# Revit family: xWELED_Ceiling Hosted_R16_V1.0
name_source: partatom
category: Lighting Fixtures
revit_build: Autodesk Revit 2016 (Build: 20150220_1215(x64)
units: mm (PartAtom-declared; Revit-internal decimal feet)

## family parameters
Always vertical = Yes
Cut with Voids When Loaded = No
Host = Ceiling
Light Source = Yes
OmniClass Number = 23.80.70.11
OmniClass Title = Luminaries for Internal Lighting
Part Type = Normal
Room Calculation Point = No
Round Connector Dimension = Use Diameter
Shared = No
Work Plane-Based = No

## types (11) — shared parameters
Charging Method = Intelligent current limited constant voltage charger
Color Filter = 16777215
Diffuser = (All directional inserts included in the box)
Dimensions L x W x H = 410mm x 100mm x 272mm
Dimming Lamp Color Temperature Shift = <None>
Operating Mode = Maintained
Operating Temperature = 1˚C to 40˚C
Tilt Angle = 90.00°

## per-type parameters (varying)
| type | AS/NZ2293 Classification | Battery | Catalogue Number | Construction | Description | IP Rating | Impact Rating | Lamp | Mounting | Operating Voltage | Photometric Web File | Power Consumption | Testing System | Viewing Distance |
| CWELED-ZW | C0=E2 C90=E2 |  | LWELED-ZW | Base Material: GRP
Diffuser Cover Material: Polycarbonate | LED L10 OPTIMUM Ceiling Mount IP65 Weatherproof Exit, 24 metre viewing Distance | IP65 | IK08 | 6 x high intensity, low energy LED, surface mounted onto a replaceable lamp bar - 100,000hour | Ceiling Mount, Single & Double Sided | 240V | ll19244-r01 - CWELED-ZW.IES | 2.7W (standby) 4.7W (max during 16 hour charge) | Zoneworks Computerised Testing |  |
| CWELED | C0=E2 C90=E2 | Lithium Iron Phosphate, 3.2V 1500mAh | CWELED | Polycarbonate Clear Cover, Glass Reinforced Nylon PA66 Base | LP Premium Weatherproof Emergency Exit, Enabled with Clevertest Plus | IP66/IP67 | IK10 | 6 x lLED lamp bar - 100,000 hours | Wall, Ceiling Mount, Single & Double Sided | 240V AC; 50Hz | ll19244-r01 - CWELED-ZW.IES | 2.6W (standby) 5.1W (max) | Clevertest Plus Enabled (not activated by default) | 24m |
| CWELED-A | C0=E2 C90=E2 | Lithium Iron Phosphate, 3.2V 1500mAh | CWELED-A | Acrylic Clear Cover, Glass Reinforced Nylon PA66 Base | LP Premium Weatherproof Emergency Exit with Acrylic Cover, Enabled with Clevertest Plus | IP66/IP67 | IK10 | 6 x lLED lamp bar - 100,000 hours | Wall, Ceiling Mount, Single & Double Sided | 240V AC; 50Hz | ll19244-r01 - CWELED-ZW.IES | 2.6W (standby) 5.1W (max) | Clevertest Plus Enabled (not activated by default) | 24m |
| CWELED-TP | C0=E2 C90=E2 | Lithium Iron Phosphate, 3.2V 1500mAh | CWELED-TP | Polycarbonate Cover, Glass Reinforced Nylon PA66 Base | LP Premium Weatherproof Emergency Exit and tamperproof screws, Enabled with Clevertest Plus | IP66/IP67 | IK10 | 6 x lLED lamp bar - 100,000 hours | Wall, Ceiling Mount, Single & Double Sided | 240V AC; 50Hz | ll19244-r01 - CWELED-ZW.IES | 2.6W (standby) 5.1W (max) | Clevertest Plus Enabled (not activated by default) | 24m |
| CWELED-DALI | C0=E2 C90=E2 | Lithium Iron Phosphate, 3.2V 1500mAh | CWELED-DALI | Polycarbonate Clear Cover, Glass Reinforced Nylon PA66 Base | LP Premium Weatherproof Emergency Exit | IP66/IP67 | IK10 | 6 x lLED lamp bar - 100,000 hours | Wall, Ceiling Mount, Single & Double Sided | 240V AC; 50Hz | ll19244-r01 - CWELED-ZW.IES | 2.6W (standby) 5.1W (max) | DALI Compatible | 24m |
| CWELED-DATA | C0=E2 C90=E2 | Lithium Iron Phosphate, 3.2V 1500mAh | CWELED-DATA | Polycarbonate Clear Cover, Glass Reinforced Nylon PA66 Base | LP Premium Weatherproof Emergency Exit | IP66/IP67 | IK10 | 6 x lLED lamp bar - 100,000 hours | Wall, Ceiling Mount, Single & Double Sided | 240V AC; 50Hz | ll19244-r01 - CWELED-ZW.IES | 2.6W (standby) 5.1W (max) | Zoneworks DATA | 24m |
| LWELED | C0=E2 C90=E2 | Lithium Nonophosphate, 3.3V 2500mAh | LWELED | Polycarbonate Clear Cover, Glass Reinforced Nylon PA66 Base | L10 Lithium Nanophosphate Weatherproof Emergency Exit, Enabled with Clevertest Plus | IP66/IP67 | IK10 | 6 x LED lamp bar - 100,000 hours | Wall, Ceiling Mount, Single & Double Sided | 240V AC; 50Hz | ll19243 - LWELED-ZW.IES | 2.7W (standby) 4.5W (max) | Clevertest Plus Enabled (not activated by default) | 24m |
| LWELED-ZW | C0=E2 C90=E2 | Lithium Nanophosphate, 3.3V 2500mAh | LWELED-ZW | Polycarbonate Clear Cover, Glass Reinforced Nylon PA66 Base | L10 Optimum Weatherproof Emergency Exit | IP66/IP67 | IK10 | 6 x LED lamp bar - 100,000 hours | Wall, Ceiling Mount, Single & Double Sided | 240V AC; 50Hz | ll19243 - LWELED-ZW.IES | 2.7W (standby) 4.5W (max) | Zoneworks Computer Testing | 24m |
| LWELED-DALI | C0=E2 C90=E2 | Lithium Nanophosphate, 3.3V 2500mAh | LWELED-DALI | Polycarbonate Clear Cover, Glass Reinforced Nylon PA66 Base | L10 Optimum Weatherproof Emergency Exit | IP66/IP67 | IK10 | 6 x LED lamp bar - 100,000 hours | Wall, Ceiling Mount, Single & Double Sided | 240V AC; 50Hz | ll19243 - LWELED-ZW.IES | 2.7W (standby) 4.5W (max) | DALI Compatible | 24m |
| LWELED-DATA | C0=E2 C90=E2 | Lithium Nanophosphate, 3.3V 2500mAh | LWELED-DATA | Polycarbonate Clear Cover, Glass Reinforced Nylon PA66 Base | L10 Optimum Weatherproof Emergency Exit | IP66/IP67 | IK10 | 6 x LED lamp bar - 100,000 hours | Wall, Ceiling Mount, Single & Double Sided | 240V AC; 50Hz | ll19243 - LWELED-ZW.IES | 2.7W (standby) 4.5W (max) | Zoneworks DATA computurised testing | 24m |
| EWELED-LI | C0=E2 C90=E1.6 | Lithium Iron Phosphate, 3.2V 600mAh | EWELED-LI | Polycarbonate Clear Cover, Glass Reinforced Nylon PA66 Base | Economy Weatherproof Emergency Exit | IP66/IP67 | IK10 | 4 x LED lamp bar - 50,000 hours | Wall, Ceiling Mount, Single & Double Sided | 240V AC; 50Hz | ll20171 - EWELED-LI.IES | 1.1W (standby) 2.0W (max) | N/A - Manual Test Switch | 24m |

## geometry (parser evidence)
native form markers: Sweep x2
no freeform markers — native parametric forms only
